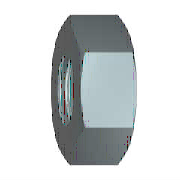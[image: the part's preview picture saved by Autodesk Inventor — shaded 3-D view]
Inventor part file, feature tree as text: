
AUTODESK INVENTOR PART (.ipt)
format: ipt  version: 2017 SP1 (Build 210196100, 196)  size: 162,304 bytes
history: native  units: mm (DEFAULTED — no unit token found)
features: sketch x3, chamfer x1, hole x1, other x1, plane x1
ambient origin geometry x7: Origin, YZ Plane, XZ Plane, X Axis, Y Axis, Z Axis, Center Point
bodies: Solid1 (feature_tree), Body (feature_tree)
feature tree (7):
  chamfer  "Chamfer1"  Angle=30.0deg  [1 undecoded]
  hole  "Thread"  [1 undecoded]
  other  "Work Axis1"
  plane  "Work Plane1"
  sketch  "Sketch1"  dims[d0=6.350853mm]
  sketch  "Sketch2"  dims[d1=2.4mm]
  sketch  "Sketch3"  dims[d2=0.0mm d3=30.0deg d4=30.0deg d5=4.6mm d6=4.6mm d7=90.0deg d25=2.459mm d26=6.0mm d27=4.0mm d28=2.0mm d29=14.3117mm d30=8.0mm d31=20.594885mm d8=0.270633mm d9=30.0deg d10=0.270633mm d11=30.0deg d13=0.0mm d14=0.0mm d39=0.0mm d40=0.270633mm d41=0.270633mm d42=0.0mm]
note: 2 required parameter values undecoded (feature->parameter linkage not recoverable at this tier; creation-order binding heuristic only, values carry confidence <= 0.55)
